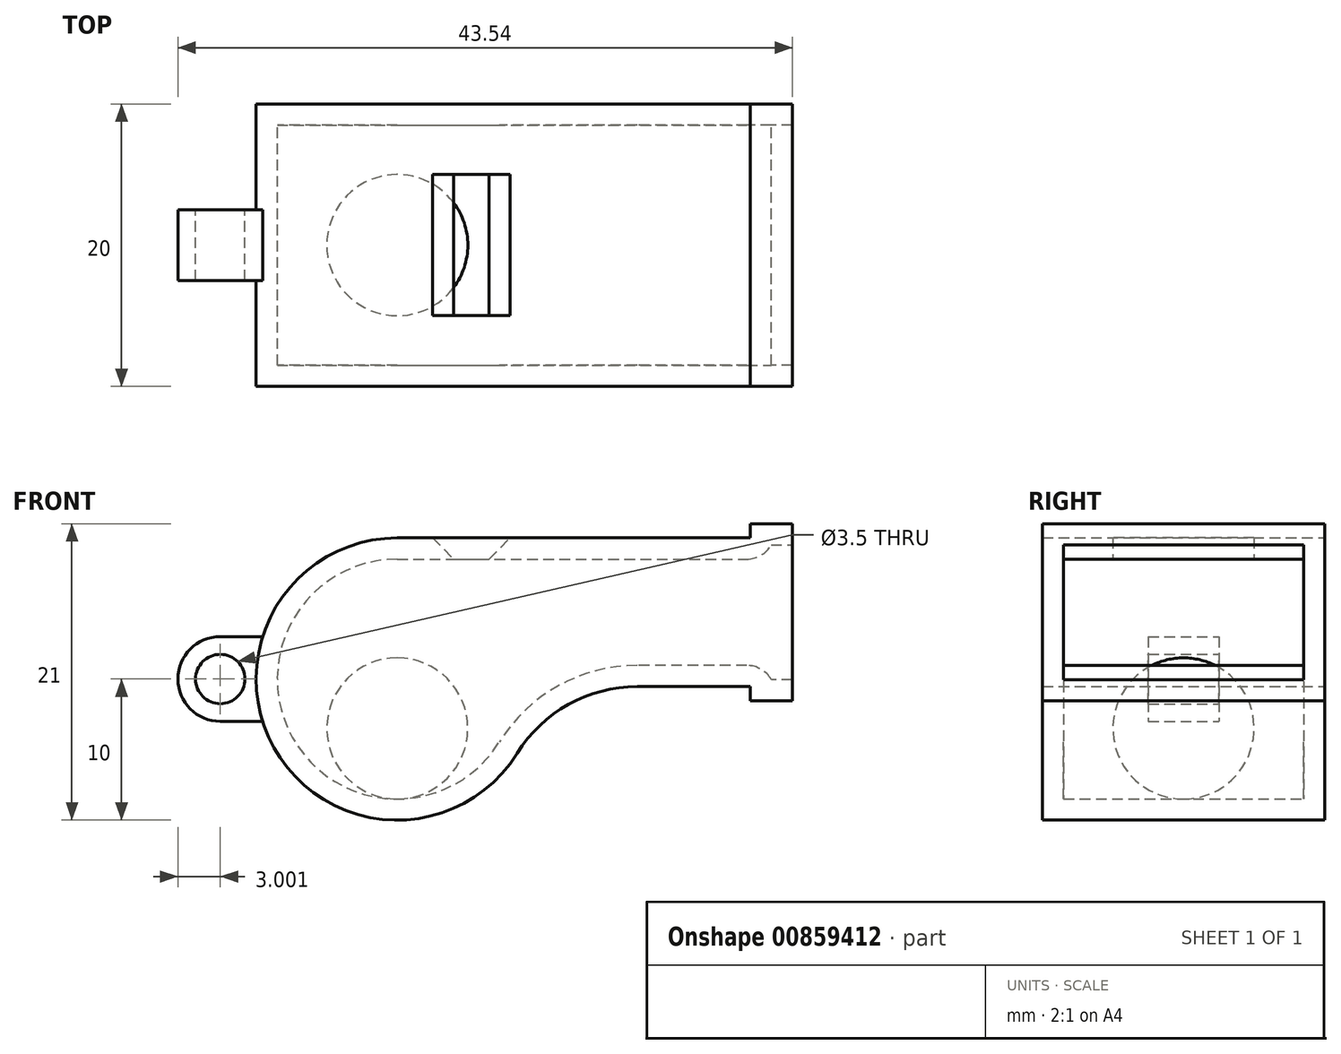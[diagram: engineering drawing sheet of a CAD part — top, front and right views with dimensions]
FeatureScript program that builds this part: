
annotation { "Feature Type Name" : "Feature", "Feature Type Description" : "" }
export const myFeature = defineFeature(function(context is Context, id is Id, definition is map)
    precondition{}
    {
        {
            var Q0;
            Q0=qCreatedBy(makeId("Front.planeOp"),FACE);
            var sketch = newSketch(context, id + "F0", { "sketchPlane" : qUnion([Q0])});
            skArc(sketch, "E0", {"start": v(0, 10) * mm, "mid": v(-8.74, -4.86) * mm, "end": v(8.5, -5.27) * mm});
            skLineSegment(sketch, "E1", {"start": v(0, 10) * mm, "end": v(25, 10) * mm});
            skLineSegment(sketch, "E2", {"start": v(25, 10) * mm, "end": v(25, 11) * mm});
            skLineSegment(sketch, "E3", {"start": v(25, 11) * mm, "end": v(28, 11) * mm});
            skLineSegment(sketch, "E4", {"start": v(28, 11) * mm, "end": v(28, -1.54) * mm});
            skLineSegment(sketch, "E5", {"start": v(28, -1.54) * mm, "end": v(25, -1.54) * mm});
            skLineSegment(sketch, "E6", {"start": v(25, -1.54) * mm, "end": v(25, -0.54) * mm});
            skLineSegment(sketch, "E7", {"start": v(25, -0.54) * mm, "end": v(17, -0.54) * mm});
            skPoint(sketch, "E8.visualSharp", {"position": v(9.99, -0.54) * mm});
            skArc(sketch, "E8.filletArc", {"start": v(17, -0.54) * mm, "mid": v(12.14, -1.8) * mm, "end": v(8.5, -5.27) * mm});
            skSolve(sketch);
        }
        {
            var Q0;
            Q0 = qSketchRegion(id + "F0", true);
            extrude(context, id + "F1", {"entities" : qUnion([Q0]), "endBound" : BoundingType.SYMMETRIC, "depth" : 20 * mm, "offsetDistance" : 25 * mm});
        }
        {
            var Q0;
            Q0=makeQuery(id+"F1.opExtrude","SWEPT_FACE",FACE,{"disambiguationData":[OSD([sQuery(id+"F0.wireOp",EDGE,"E4")])]});
            shell(context, id + "F2", {"entities" : qUnion([Q0]), "thickness" : 1.5 * mm});
        }
        {
            var Q0;
            Q0=qCreatedBy(makeId("Front.planeOp"),FACE);
            var sketch = newSketch(context, id + "F3", { "sketchPlane" : qUnion([Q0])});
            skLineSegment(sketch, "E9", {"start": v(2.5, 10) * mm, "end": v(4, 8.5) * mm});
            skLineSegment(sketch, "E10", {"start": v(4, 8.5) * mm, "end": v(6.5, 8.5) * mm});
            skLineSegment(sketch, "E11", {"start": v(6.5, 8.5) * mm, "end": v(8, 10) * mm});
            skLineSegment(sketch, "E12", {"start": v(2.5, 10) * mm, "end": v(8, 10) * mm});
            skSolve(sketch);
        }
        {
            var Q0;
            Q0 = qSketchRegion(id + "F3", true);
            extrude(context, id + "F4", {"entities" : qUnion([Q0]), "operationType" : NewBodyOperationType.REMOVE, "endBound" : BoundingType.SYMMETRIC, "oppositeDirection" : true, "depth" : 10 * mm, "offsetDistance" : 25 * mm});
        }
        {
            var Q0;
            Q0=qCreatedBy(makeId("Front.planeOp"),FACE);
            var sketch = newSketch(context, id + "F5", { "sketchPlane" : qUnion([Q0])});
            skCircle(sketch, "E13", {"center": v(-12.54, 0) * mm, "radius": 1.75 * mm});
            skArc(sketch, "E14", {"start": v(-12.54, 3) * mm, "mid": v(-15.54, 0) * mm, "end": v(-12.54, -3) * mm});
            skLineSegment(sketch, "E15", {"start": v(-12.54, 3) * mm, "end": v(-9.54, 3) * mm});
            skLineSegment(sketch, "E16", {"start": v(-9.54, 3) * mm, "end": v(-9.54, -3) * mm});
            skLineSegment(sketch, "E17", {"start": v(-9.54, -3) * mm, "end": v(-12.54, -3) * mm});
            skSolve(sketch);
        }
        {
            var Q0;
            Q0 = qSketchRegion(id + "F5", true);
            extrude(context, id + "F6", {"entities" : qUnion([Q0]), "operationType" : NewBodyOperationType.ADD, "endBound" : BoundingType.SYMMETRIC, "depth" : 5 * mm, "offsetDistance" : 25 * mm});
        }
        {
            var Q0;
            Q0=qCreatedBy(makeId("Front.planeOp"),FACE);
            var sketch = newSketch(context, id + "F7", { "sketchPlane" : qUnion([Q0])});
            skArc(sketch, "E18", {"start": v(0, -8.5) * mm, "mid": v(5, -3.5) * mm, "end": v(0, 1.5) * mm});
            skLineSegment(sketch, "E19", {"start": v(0, 1.5) * mm, "end": v(0, -8.5) * mm});
            skSolve(sketch);
        }
        {
            var Q0;
            Q0 = qSketchRegion(id + "F7", true);
            var Q1;
            Q1=sQuery(id+"F7.wireOp",EDGE,"E19");
            var Q2;
            Q2=sQuery(id+"F7.wireOp",EDGE,"E18");
            var Q3;
            Q3=sQuery(id+"F7.wireOp",EDGE,"E19");
            revolve(context, id + "F8", {"surfaceOperationType" : NewSurfaceOperationType.NEW, "entities" : qUnion([Q0]), "surfaceEntities" : qUnion([Q1, Q2]), "axis" : qUnion([Q3]), "revolveType" : RevolveType.FULL});
        }
        {
            var Q0;
            Q0=makeQuery(id+"F2.opShell","OFFSET_EDGE",EDGE,{"disambiguationData":[OSD([sQuery(id+"F0.wireOp",EDGE,"E6"),sQuery(id+"F0.wireOp",EDGE,"E7")])]});
            var Q1;
            Q1=makeQuery(id+"F2.opShell","OFFSET_EDGE",EDGE,{"disambiguationData":[OSD([sQuery(id+"F0.wireOp",EDGE,"E1"),sQuery(id+"F0.wireOp",EDGE,"E2")])]});
            fillet(context, id + "F9", {"entities" : qUnion([Q0, Q1]), "radius" : 2 * mm, "tangentPropagation" : true, "allowEdgeOverflow" : false});
        }
    });
